# Revit family: Building-IEC309Connections-GEWISS-IEC309HP-90°_SURF_MOUNT_INLET_32A_IP67
name_source: partatom
category: Apparecchi elettrici
units: mm (PartAtom-declared; Revit-internal decimal feet)

## family parameters
Condiviso = Sì
Host = Superficie
Mantenere orientamento annotazione = Sì
Punto di calcolo locali = Sì
Quota connettore circolare = Usa diametro
Taglio con vuoti quando caricato = No
Tipo di parte = Normale

## types (12) — shared parameters
BLOCCO = B=C
Breaking capacity at 1.1 Un = 40A
Catalogue = BUILDING
Corpo centrale = Default(2)
FORMULA = 1000 mm  [stored 3.28084 ft]
Frequency = 50/60 Hz
Glow wire test: = 850 °C (active parts) - 650 °C (passive parts)
IDF = f9afb612-cbf0-4888-a81a-e499d037be71
IDT = 00b3c0f90a2441e8b989aa4ccf7db640
IP degree = IP67
Immagine tipo = <Nessuno>
Insulation resistance = - 10 M?
L = 155 mm
Operating temperature: = -25 +55 °C
Permissible overload = 42A
Piastra = Default(2)
Produttore = GEWISS S.p.A.
Prospetto di default = 1219 mm
Rated current (A) = 32
SEO = Inlet
SPinotto = Default(2)
Shock resistance = IK08
Spostamento_S = 953 mm
Technical sheet = https://www.gewiss.com
Terminal tightening capacity = 2.5-6mm² flexible cables - 2.5-10mm² rigid cables
Thermo-pressure with ball = 125 °C (active parts) - 80 °C (passive parts)
Total number of operations = -2000
Type of wiring = With screw
Typology = 90° angled surface mounting inlet
URL = https://www.gewiss.com
Version file RFA = 21.11
W = 115 mm

## per-type parameters (varying)
| type | Colour: | Descrizione | Electrocod | Modello | No. of poles | Rated voltage | Reference h |
| GW60439 - IP67 90°APPL.INLET 3P+N+E 32A 230V 9H | Blue | IP67 90°APPL.INLET 3P+N+E 32A 230V 9H | 2230 | GW60439 | 3P+N+E | 200-250V | 9 |
| GW60442 - IP67 90°APPL.INLET 3P+N+E 32A 400V 6H | Red | IP67 90°APPL.INLET 3P+N+E 32A 400V 6H | 2230 | GW60442 | 3P+N+E | 380-415V | 6 |
| GW60437 - IP67 90°APPL.INLET 2P+E 32A 230V 6H | Blue | IP67 90°APPL.INLET 2P+E 32A 230V 6H | 2230 | GW60437 | 2P+E | 200-250V | 6 |
| GW60441 - IP67 90°APPL.INLET 3P+E 32A 400V 6H | Red | IP67 90°APPL.INLET 3P+E 32A 400V 6H | 2230 | GW60441 | 3P+E | 380-415V | 6 |
| GW60434 - IP67 90°APPL.INLET 2P+E 32A 110V 4H | Yellow | IP67 90°APPL.INLET 2P+E 32A 110V 4H | 2230 | GW60434 | 2P+E | 100-130V | 4 |
| GW60436 - IP67 90°APPL.INLET 3P+N+E 32A 110V 4H | Yellow | IP67 90°APPL.INLET 3P+N+E 32A 110V 4H | 2230 | GW60436 | 3P+N+E | 100-130V | 4 |
| GW60482 - IP67 90°APPL.INLET 3P+E 32A 380V 3H | Red | IP67 90°APPL.INLET 3P+E 32A 380V 3H | 2231 | GW60482 | 3P+E | 380-440V | 3 |
| GW60440 - IP67 90°APPL.INLET 2P+E 32A 400V 9H | Red | IP67 90°APPL.INLET 2P+E 32A 400V 9H | 2230 | GW60440 | 2P+E | 380-415V | 9 |
| GW60435 - IP67 90°APPL.INLET 3P+E 32A 110V 4H | Yellow | IP67 90°APPL.INLET 3P+E 32A 110V 4H | 2230 | GW60435 | 3P+E | 100-130V | 4 |
| GW60443 - IP67 90°APPL.INLET 3P+E 32A 500V 7H | Black | IP67 90°APPL.INLET 3P+E 32A 500V 7H | 2230 | GW60443 | 3P+E | 480-500V | 7 |
| GW60438 - IP67 90°APPL.INLET 3P+E 32A 230V 9H | Blue | IP67 90°APPL.INLET 3P+E 32A 230V 9H | 2230 | GW60438 | 3P+E | 200-250V | 9 |
| GW60444 - IP67 90°APPL.INLET 3P+N+E 32A 500V 7H | Black | IP67 90°APPL.INLET 3P+N+E 32A 500V 7H | 2230 | GW60444 | 3P+N+E | 480-500V | 7 |

note: [stored X ft] marks values corroborated as IEEE doubles in the binary element streams (Revit-internal decimal feet)

## geometry (parser evidence)
native form markers: Sweep x1
no freeform markers — native parametric forms only
